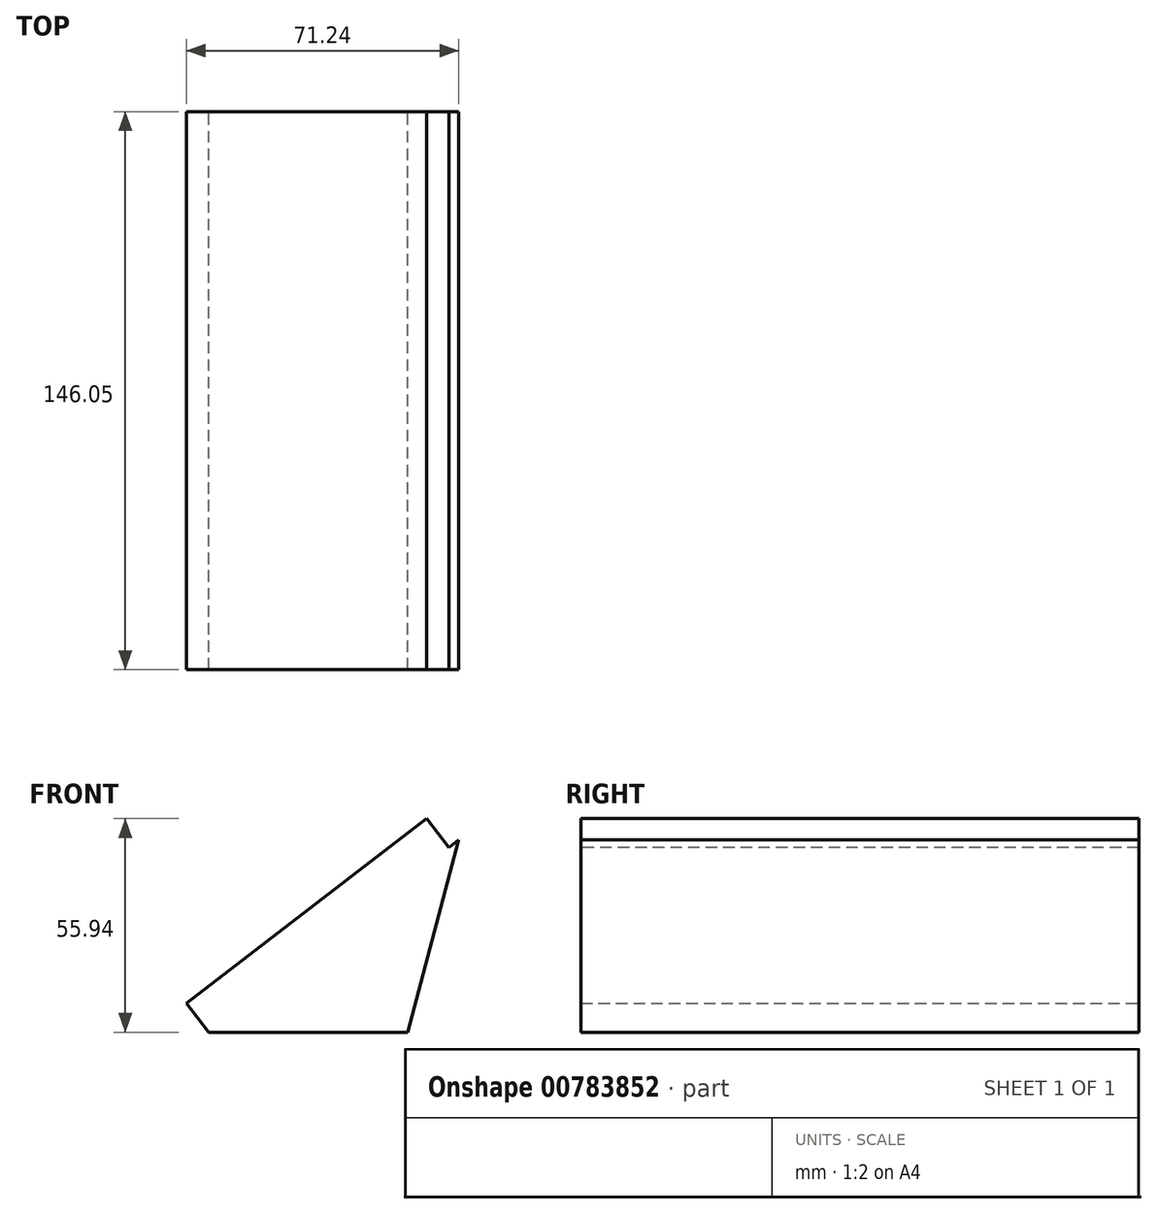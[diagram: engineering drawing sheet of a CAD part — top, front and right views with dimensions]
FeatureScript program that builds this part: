
annotation { "Feature Type Name" : "Feature", "Feature Type Description" : "" }
export const myFeature = defineFeature(function(context is Context, id is Id, definition is map)
    precondition{}
    {
        {
            var Q0;
            Q0=qCreatedBy(makeId("Front.planeOp"),FACE);
            var sketch = newSketch(context, id + "F0", { "sketchPlane" : qUnion([Q0])});
            skLineSegment(sketch, "E0", {"start": v(-79.76, -44.64) * mm, "end": v(-14.33, 5.69) * mm});
            skLineSegment(sketch, "E1", {"start": v(-14.33, 5.69) * mm, "end": v(-27.69, -44.64) * mm});
            skLineSegment(sketch, "E2", {"start": v(-27.69, -44.64) * mm, "end": v(-79.76, -44.64) * mm});
            skLineSegment(sketch, "E3", {"start": v(-27.69, -44.64) * mm, "end": v(-47.05, -19.48) * mm, "construction": true});
            skSolve(sketch);
        }
        {
            var Q0;
            Q0=makeQuery(id+"F0.imprint","IMPRINT",FACE,{"disambiguationData":[TD([[makeQuery(id+"F0.imprint","IMPRINT",EDGE,{"derivedFrom":sQuery(id+"F0.wireOp",EDGE,"E0")}),-1.0]])]});
            extrude(context, id + "F1", {"entities" : qUnion([Q0]), "depth" : 146.05 * mm, "offsetDistance" : 25.4 * mm});
        }
        {
            var Q0;
            Q0=makeQuery(id+"F1.opExtrude","SWEPT_FACE",FACE,{"disambiguationData":[OSD([sQuery(id+"F0.wireOp",EDGE,"E0")])]});
            var sketch = newSketch(context, id + "F2", { "sketchPlane" : qUnion([Q0])});
            skLineSegment(sketch, "E4.bottom", {"start": v(-11.06, 0) * mm, "end": v(-90.44, 0) * mm});
            skLineSegment(sketch, "E4.top", {"start": v(-11.06, -146.05) * mm, "end": v(-90.44, -146.05) * mm});
            skLineSegment(sketch, "E4.left", {"start": v(-11.06, 0) * mm, "end": v(-11.06, -146.05) * mm});
            skLineSegment(sketch, "E4.right", {"start": v(-90.44, 0) * mm, "end": v(-90.44, -146.05) * mm});
            skSolve(sketch);
        }
        {
            var Q0;
            Q0=makeQuery(id+"F2.imprint","IMPRINT",FACE,{"disambiguationData":[TD([[makeQuery(id+"F2.imprint","IMPRINT",EDGE,{"derivedFrom":sQuery(id+"F2.wireOp",EDGE,"E4.bottom")}),-1.0]])]});
            extrude(context, id + "F3", {"entities" : qUnion([Q0]), "operationType" : NewBodyOperationType.ADD, "depth" : 9.52 * mm, "offsetDistance" : 25.4 * mm});
        }
    });
